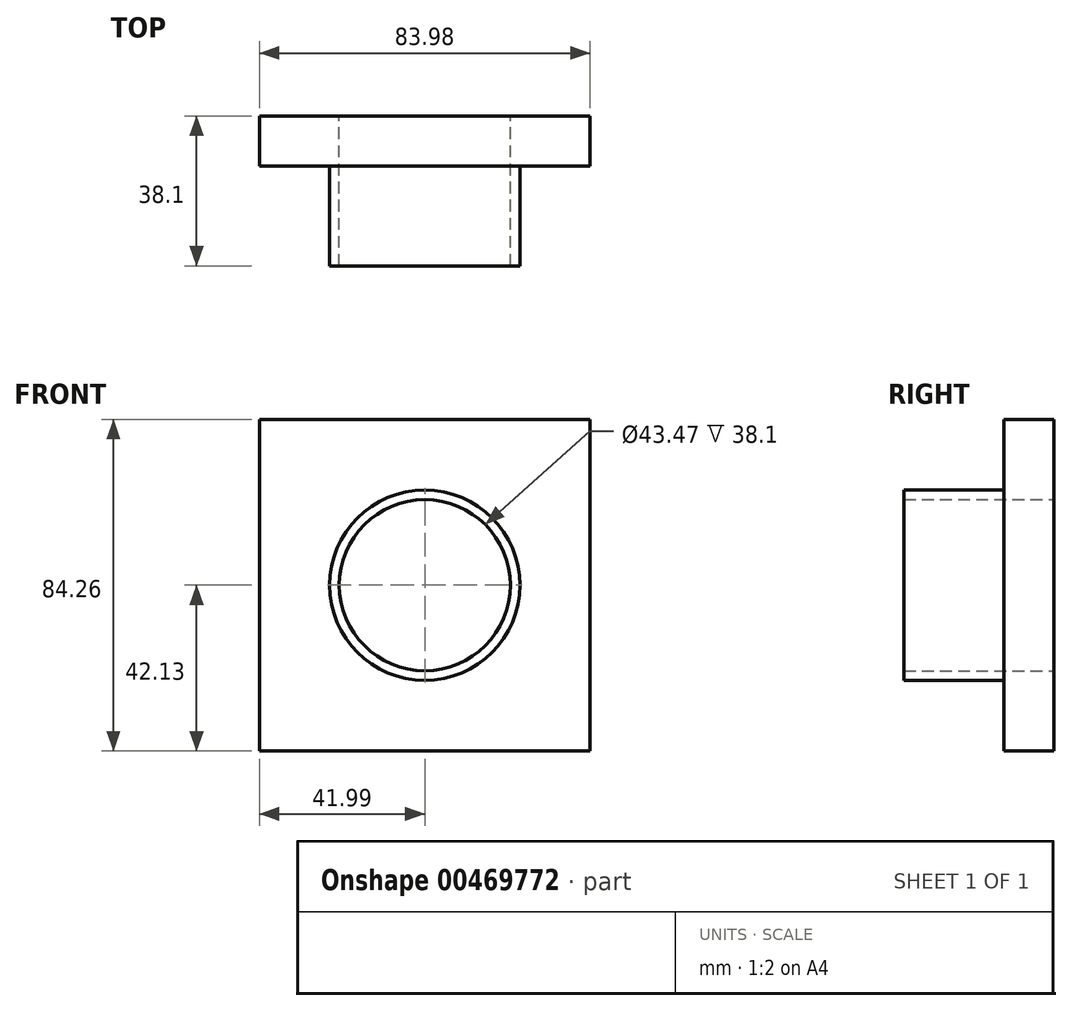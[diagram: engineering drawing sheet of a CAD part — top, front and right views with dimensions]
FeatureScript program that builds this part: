
annotation { "Feature Type Name" : "Feature", "Feature Type Description" : "" }
export const myFeature = defineFeature(function(context is Context, id is Id, definition is map)
    precondition{}
    {
        {
            var Q0;
            Q0=qCreatedBy(makeId("Front.planeOp"),FACE);
            var sketch = newSketch(context, id + "F0", { "sketchPlane" : qUnion([Q0])});
            skLineSegment(sketch, "E0.bottom", {"start": v(-42, 42.13) * mm, "end": v(42, 42.13) * mm});
            skLineSegment(sketch, "E0.top", {"start": v(-42, -42.13) * mm, "end": v(42, -42.13) * mm});
            skLineSegment(sketch, "E0.left", {"start": v(-42, 42.13) * mm, "end": v(-42, -42.13) * mm});
            skLineSegment(sketch, "E0.right", {"start": v(42, 42.13) * mm, "end": v(42, -42.13) * mm});
            skPoint(sketch, "E0.middle", {"position": v(0, 0) * mm});
            skCircle(sketch, "E1", {"center": v(0, 0) * mm, "radius": 21.74 * mm});
            skCircle(sketch, "E2", {"center": v(0, 0) * mm, "radius": 18.58 * mm});
            skSolve(sketch);
        }
        {
            var Q0;
            Q0=makeQuery(id+"F0.imprint","IMPRINT",FACE,{"disambiguationData":[TD([[makeQuery(id+"F0.imprint","IMPRINT",EDGE,{"derivedFrom":sQuery(id+"F0.wireOp",EDGE,"E0.bottom")}),-1.0]])]});
            extrude(context, id + "F1", {"entities" : qUnion([Q0]), "depth" : 12.7 * mm});
        }
        {
            var Q0;
            Q0=makeQuery(id+"F1.opExtrude","CAP_FACE",FACE,{"disambiguationData":[OSD([sQuery(id+"F0.wireOp",EDGE,"E0.bottom"),sQuery(id+"F0.wireOp",EDGE,"E0.top"),sQuery(id+"F0.wireOp",EDGE,"E0.left"),sQuery(id+"F0.wireOp",EDGE,"E0.right"),sQuery(id+"F0.wireOp",EDGE,"E1")])],"isStart":false});
            var sketch = newSketch(context, id + "F2", { "sketchPlane" : qUnion([Q0])});
            skCircle(sketch, "E3", {"center": v(0, 0) * mm, "radius": 24.17 * mm});
            skSolve(sketch);
        }
        {
            var Q0;
            Q0=makeQuery(id+"F2.imprint","IMPRINT",FACE,{"disambiguationData":[TD([[makeQuery(id+"F2.imprint","IMPRINT",EDGE,{"derivedFrom":sQuery(id+"F2.wireOp",EDGE,"E3")}),1.0]])]});
            extrude(context, id + "F3", {"entities" : qUnion([Q0]), "operationType" : NewBodyOperationType.ADD, "depth" : 25.4 * mm});
        }
    });
